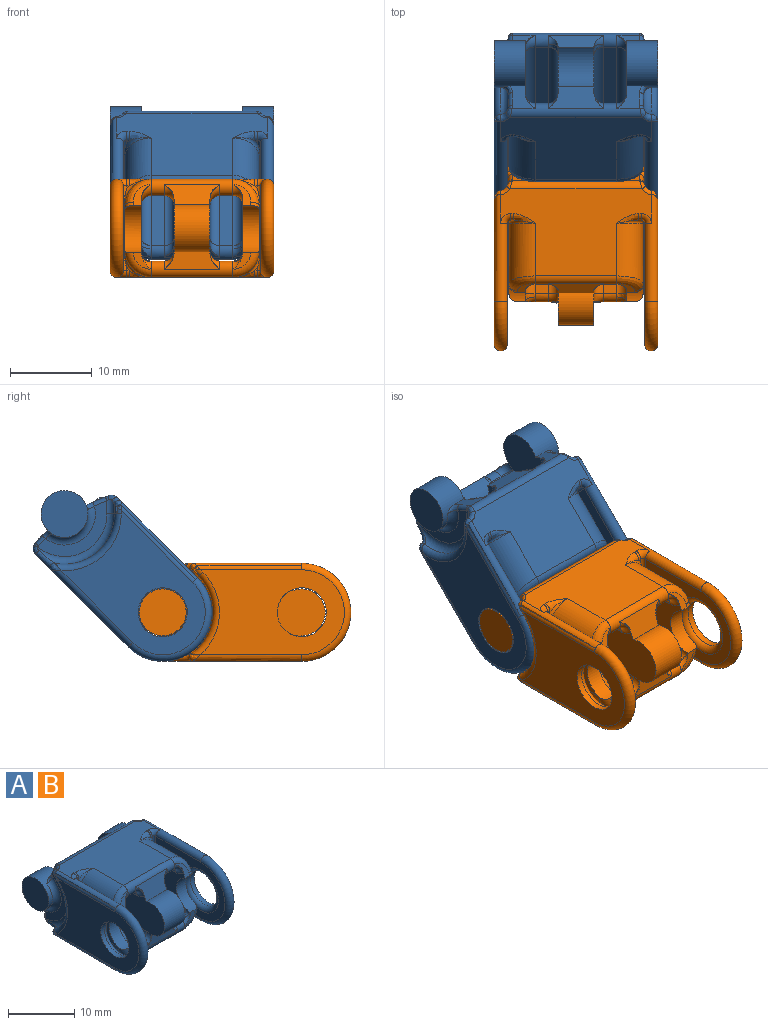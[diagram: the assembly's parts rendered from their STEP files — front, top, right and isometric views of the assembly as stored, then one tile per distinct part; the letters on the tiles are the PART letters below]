
ASSEMBLY  parts=2 mates=1
PART A: 156 faces, bbox 21.1x27x14.7 mm
  f0: plane 0.41x0.32mm, normal (0,-1,0), area 0.1mm2, adj f66,f67,f81
  f1: plane 7.26x3.08mm, normal (0,0.92,0.38), area 14mm2, adj f10,f27,f30,f47,f91,f119
  f2: plane 3.54x2.61mm, normal (0,1,0), area 4.2mm2, adj f12,f21,f29,f41,f56,f57
  f3: plane 2.19x2mm, normal (0,-1,0), area 1.8mm2, adj f5,f23,f37,f52
  f4: plane 3.08x2.66mm, normal (0,-0.92,0.38), area 2.5mm2, adj f12,f23,f42,f50,f51
  f5: plane 0.09x0.04mm, normal (-1,0,0), area 0mm2, adj f3,f23,f37
  f6: plane 0.09x0.04mm, normal (1,0,0), area 0mm2, adj f8,f27,f35
  f7: plane 7.26x2.6mm, normal (0,-1,0), area 11mm2, adj f10,f25,f31,f32,f91,f104
  f8: plane 6.8x2mm, normal (0,1,0), area 10.4mm2, adj f6,f27,f29,f35,f89,f107
  f9: plane 3.54x3.21mm, normal (0,0.92,0.38), area 5.5mm2, adj f12,f21,f30,f44,f61,f62,f63
  f10: plane 18.78x6.61mm, normal (1,0,0), area 95.3mm2, adj f1,f7,f25,f26,f27,f32,f33,f45
  f11: plane 8.52x5.6mm, normal (1,0,0), area 39.6mm2, adj f23,f48,f49,f51,f68
  f12: plane 18.78x6.61mm, normal (-1,0,0), area 95.3mm2, adj f2,f4,f9,f21,f23,f40,f41,f42
  f13: plane 14.8x10.4mm, normal (-1,0,0), area 96.9mm2, adj f67,f75,f77,f79,f83
  f14: plane 19.08x15.68mm, normal (0,0,-1), area 190.7mm2, adj f29,f31,f48,f60,f79,f80,f81,f82
  f15: plane 5.72x5.72mm, normal (1,0,0), area 25.7mm2, adj f21
  f16: plane 19.08x11.37mm, normal (0,0,1), area 134.3mm2, adj f28,f30,f49,f65,f70,f71,f74,f75
  f17: plane 10.69x1.6mm, normal (0,0,-1), area 17.1mm2, adj f28,f30,f43,f46
  f18: plane 17.6x10.4mm, normal (1,0,0), area 126.3mm2, adj f24,f73,f75,f76,f77,f79
  f19: plane 0.41x0.32mm, normal (0,-1,0), area 0.1mm2, adj f67,f69,f71
  f20: plane 15x1.6mm, normal (0,0,1), area 24mm2, adj f29,f31,f33,f34,f39,f40
  f21: cylinder r=2.86mm len=5.72mm, axis (1,0,0), area 45.4mm2, adj f2,f9,f12,f15,f55,f56,f61
  f22: plane 9.99x4.7mm, normal (1,0,0), area 16mm2, adj f53,f54,f55,f57,f58,f62
  f23: cylinder r=3mm len=5.77mm, axis (1,0,0), area 16.1mm2, adj f3,f4,f5,f11,f12,f38,f39,f48
  f24: cylinder r=3mm len=6mm, axis (1,0,0), area 15.1mm2, adj f18,f83
  f25: cylinder r=2.86mm len=5.72mm, axis (-1,0,0), area 44.5mm2, adj f7,f10,f26,f91
  f26: plane 7.26x3.2mm, normal (0,-0.92,0.38), area 14.6mm2, adj f10,f25,f28,f45,f91,f117
  f27: cylinder r=3mm len=5.77mm, axis (-1,0,0), area 36.3mm2, adj f1,f6,f8,f10,f34,f36,f89,f91
  f28: cylinder r=1mm len=10mm, axis (-1,0,0), area 18.1mm2, adj f16,f17,f26,f42,f45,f50,f96,f114
  f29: cylinder r=1mm len=15.63mm, axis (-1,0,0), area 29.5mm2, adj f2,f8,f14,f20,f35,f36,f41,f58
  f30: cylinder r=1mm len=16.18mm, axis (1,0,0), area 25mm2, adj f1,f9,f16,f17,f44,f47,f64,f90
  f31: cylinder r=1mm len=10mm, axis (-1,0,0), area 20.7mm2, adj f7,f14,f20,f32,f37,f38,f52,f99
  f32: torus R=2.2mm, axis (-1,0,0), area 2.5mm2, adj f7,f10,f31,f33
  f33: cylinder r=1.2mm len=14.92mm, axis (0,1,0), area 28.1mm2, adj f10,f20,f32,f34
  f34: bspline ~1.28x1.26mm, area 0.1mm2, adj f20,f27,f33,f36
  f35: torus R=2.2mm, axis (-1,0,0), area 1.1mm2, adj f6,f8,f29,f36
  f36: bspline ~1.41x1.35mm, area 1.1mm2, adj f27,f29,f34,f35
  f37: torus R=2.2mm, axis (-1,0,0), area 1.1mm2, adj f3,f5,f31,f38
  f38: bspline ~1.41x1.35mm, area 1.1mm2, adj f23,f31,f37,f39
  f39: bspline ~1.28x1.26mm, area 0.1mm2, adj f20,f23,f38,f40
  f40: cylinder r=1.2mm len=14.92mm, axis (0,-1,0), area 28.1mm2, adj f12,f20,f39,f41
  f41: torus R=2.2mm, axis (-1,0,0), area 2.5mm2, adj f2,f12,f29,f40
  f42: torus R=2.2mm, axis (-1,0,0), area 3.6mm2, adj f4,f12,f28,f43
  f43: cylinder r=1.2mm len=10.69mm, axis (0,1,0), area 20.2mm2, adj f12,f17,f42,f44
  f44: torus R=2.2mm, axis (-1,0,0), area 3.6mm2, adj f9,f12,f30,f43
  f45: torus R=2.2mm, axis (-1,0,0), area 3.6mm2, adj f10,f26,f28,f46
  f46: cylinder r=1.2mm len=10.69mm, axis (0,-1,0), area 20.2mm2, adj f10,f17,f45,f47
  f47: torus R=2.2mm, axis (-1,0,0), area 3.6mm2, adj f1,f10,f30,f46
  f48: cylinder r=3.2mm len=8.6mm, axis (0,1,0), area 43.2mm2, adj f11,f14,f23,f52,f66
  f49: cylinder r=3.2mm len=7.36mm, axis (0,-1,0), area 34.7mm2, adj f11,f16,f50,f69
  f50: bspline ~3.78x3.76mm, area 6mm2, adj f4,f28,f49,f51
  f51: cylinder r=1mm len=1.16mm, axis (0,0.38,0.92), area 0.8mm2, adj f4,f11,f23,f50
  f52: torus R=2.2mm, axis (0,-1,0), area 6.8mm2, adj f3,f23,f31,f48
  f53: torus R=5.2mm, axis (1,0,0), area 16.5mm2, adj f22,f54,f59,f60,f76
  f54: cylinder r=0.94mm len=1.91mm, axis (0,-0.71,-0.71), area 2.3mm2, adj f22,f53,f63,f64,f65,f73
  f55: torus R=3.8mm, axis (1,0,0), area 11.4mm2, adj f21,f22,f56,f61
  f56: bspline ~1.79x1.7mm, area 1mm2, adj f2,f21,f55,f57
  f57: cylinder r=0.5mm len=1.23mm, axis (0,0,1), area 1mm2, adj f2,f22,f56,f58
  f58: torus R=0.5mm, axis (1,0,0), area 0.2mm2, adj f22,f29,f57,f59
  f59: bspline ~1.21x0.9mm, area 0.8mm2, adj f29,f53,f58,f60
  f60: bspline ~3.69x1.74mm, area 3mm2, adj f14,f53,f59,f78
  f61: bspline ~1.7x1.65mm, area 1mm2, adj f9,f21,f55,f62
  f62: cylinder r=0.5mm len=1.72mm, axis (0,-0.38,0.92), area 1.3mm2, adj f9,f22,f61,f63
  f63: bspline ~0.57x0.53mm, area 0.3mm2, adj f9,f54,f62,f64
  f64: bspline ~1.18x1.16mm, area 0.7mm2, adj f30,f54,f63,f65
  f65: bspline ~1.11x0.99mm, area 1.1mm2, adj f16,f54,f64,f72
  f66: torus R=3.6mm, axis (0,-1,0), area 1.9mm2, adj f0,f48,f67,f68,f82
  f67: cylinder r=0.4mm len=10.4mm, axis (0,0,1), area 4mm2, adj f0,f13,f19,f66,f68,f69,f74,f80
  f68: cylinder r=0.4mm len=5.6mm, axis (0,0,1), area 1.6mm2, adj f11,f66,f67,f69
  f69: torus R=3.6mm, axis (0,-1,0), area 1.9mm2, adj f19,f49,f67,f68,f70
  f70: bspline ~3.09x1.2mm, area 1.2mm2, adj f16,f69,f71
  f71: cylinder r=0.8mm len=0.8mm, axis (-1,0,0), area 0.4mm2, adj f16,f19,f70,f74
  f72: bspline ~1.93x0.98mm, area 0.8mm2, adj f65,f73,f75
  f73: cylinder r=0.8mm len=1.37mm, axis (0,-0.71,-0.71), area 1mm2, adj f18,f54,f72,f76
  f74: torus R=1.2mm, axis (0,0,1), area 1.4mm2, adj f16,f67,f71,f75
  f75: cylinder r=0.8mm len=13.11mm, axis (0,-1,0), area 28.1mm2, adj f13,f16,f18,f72,f74,f77
  f76: torus R=6.94mm, axis (-1,0,0), area 13.7mm2, adj f18,f53,f73,f78
  f77: torus R=5.2mm, axis (-1,0,0), area 45.1mm2, adj f13,f18,f75,f79
  f78: bspline ~2.51x1.15mm, area 1mm2, adj f60,f76,f79
  f79: cylinder r=0.8mm len=13.28mm, axis (0,1,0), area 28.2mm2, adj f13,f14,f18,f77,f78,f80
  f80: torus R=1.2mm, axis (0,0,1), area 1.4mm2, adj f14,f67,f79,f81
  f81: cylinder r=0.8mm len=0.8mm, axis (1,0,0), area 0.4mm2, adj f0,f14,f80,f82
  f82: bspline ~3.09x1.2mm, area 1.1mm2, adj f14,f66,f81
  f83: torus R=3.8mm, axis (-1,0,0), area 26mm2, adj f13,f24
  f84: plane 0.41x0.32mm, normal (0,-1,0), area 0.1mm2, adj f138,f139,f153
  f85: plane 3.54x2.61mm, normal (0,1,0), area 4.2mm2, adj f29,f93,f100,f113,f128,f129
  f86: plane 2.19x2mm, normal (0,-1,0), area 1.8mm2, adj f88,f102,f109,f124
  f87: plane 3.08x2.66mm, normal (0,-0.92,0.38), area 2.5mm2, adj f93,f102,f114,f122,f123
  f88: plane 0.09x0.04mm, normal (1,0,0), area 0mm2, adj f86,f102,f109
  f89: plane 0.09x0.04mm, normal (-1,0,0), area 0mm2, adj f8,f27,f107
  f90: plane 3.54x3.21mm, normal (0,0.92,0.38), area 5.5mm2, adj f30,f93,f100,f116,f133,f134,f135
  f91: plane 18.78x6.61mm, normal (-1,0,0), area 95.3mm2, adj f1,f7,f25,f26,f27,f104,f105,f117
  f92: plane 8.52x5.6mm, normal (-1,0,0), area 39.6mm2, adj f102,f120,f121,f123,f140
  f93: plane 18.78x6.61mm, normal (1,0,0), area 95.3mm2, adj f85,f87,f90,f100,f102,f112,f113,f114
  f94: plane 14.8x10.4mm, normal (1,0,0), area 96.9mm2, adj f139,f147,f149,f151,f155
  f95: plane 5.72x5.72mm, normal (-1,0,0), area 25.7mm2, adj f100
  f96: plane 10.69x1.6mm, normal (0,0,-1), area 17.1mm2, adj f28,f30,f115,f118
  f97: plane 17.6x10.4mm, normal (-1,0,0), area 126.3mm2, adj f103,f145,f147,f148,f149,f151
  f98: plane 0.41x0.32mm, normal (0,-1,0), area 0.1mm2, adj f139,f141,f143
  f99: plane 15x1.6mm, normal (0,0,1), area 24mm2, adj f29,f31,f105,f106,f111,f112
  f100: cylinder r=2.86mm len=5.72mm, axis (-1,0,0), area 45.4mm2, adj f85,f90,f93,f95,f127,f128,f133
  f101: plane 9.99x4.7mm, normal (-1,0,0), area 16mm2, adj f125,f126,f127,f129,f130,f134
  f102: cylinder r=3mm len=5.77mm, axis (-1,0,0), area 16.1mm2, adj f86,f87,f88,f92,f93,f110,f111,f120
  f103: cylinder r=3mm len=6mm, axis (-1,0,0), area 15.1mm2, adj f97,f155
  f104: torus R=2.2mm, axis (1,0,0), area 2.5mm2, adj f7,f31,f91,f105
  f105: cylinder r=1.2mm len=14.92mm, axis (0,1,0), area 28.1mm2, adj f91,f99,f104,f106
  f106: bspline ~1.28x1.26mm, area 0.1mm2, adj f27,f99,f105,f108
  f107: torus R=2.2mm, axis (1,0,0), area 1.1mm2, adj f8,f29,f89,f108
  f108: bspline ~1.41x1.35mm, area 1.1mm2, adj f27,f29,f106,f107
  f109: torus R=2.2mm, axis (1,0,0), area 1.1mm2, adj f31,f86,f88,f110
  f110: bspline ~1.41x1.35mm, area 1.1mm2, adj f31,f102,f109,f111
  f111: bspline ~1.28x1.26mm, area 0.1mm2, adj f99,f102,f110,f112
  f112: cylinder r=1.2mm len=14.92mm, axis (0,-1,0), area 28.1mm2, adj f93,f99,f111,f113
  f113: torus R=2.2mm, axis (1,0,0), area 2.5mm2, adj f29,f85,f93,f112
  f114: torus R=2.2mm, axis (1,0,0), area 3.6mm2, adj f28,f87,f93,f115
  f115: cylinder r=1.2mm len=10.69mm, axis (0,1,0), area 20.2mm2, adj f93,f96,f114,f116
  f116: torus R=2.2mm, axis (1,0,0), area 3.6mm2, adj f30,f90,f93,f115
  f117: torus R=2.2mm, axis (1,0,0), area 3.6mm2, adj f26,f28,f91,f118
  f118: cylinder r=1.2mm len=10.69mm, axis (0,-1,0), area 20.2mm2, adj f91,f96,f117,f119
  f119: torus R=2.2mm, axis (1,0,0), area 3.6mm2, adj f1,f30,f91,f118
  f120: cylinder r=3.2mm len=8.6mm, axis (0,1,0), area 43.2mm2, adj f14,f92,f102,f124,f138
  f121: cylinder r=3.2mm len=7.36mm, axis (0,-1,0), area 34.7mm2, adj f16,f92,f122,f141
  f122: bspline ~3.78x3.76mm, area 6mm2, adj f28,f87,f121,f123
  f123: cylinder r=1mm len=1.16mm, axis (0,0.38,0.92), area 0.8mm2, adj f87,f92,f102,f122
  f124: torus R=2.2mm, axis (0,-1,0), area 6.8mm2, adj f31,f86,f102,f120
  f125: torus R=5.2mm, axis (-1,0,0), area 16.5mm2, adj f101,f126,f131,f132,f148
  f126: cylinder r=0.94mm len=1.91mm, axis (0,-0.71,-0.71), area 2.3mm2, adj f101,f125,f135,f136,f137,f145
  f127: torus R=3.8mm, axis (-1,0,0), area 11.4mm2, adj f100,f101,f128,f133
  f128: bspline ~1.79x1.7mm, area 1mm2, adj f85,f100,f127,f129
  f129: cylinder r=0.5mm len=1.23mm, axis (0,0,1), area 1mm2, adj f85,f101,f128,f130
  f130: torus R=0.5mm, axis (-1,0,0), area 0.2mm2, adj f29,f101,f129,f131
  f131: bspline ~1.21x0.9mm, area 0.8mm2, adj f29,f125,f130,f132
  f132: bspline ~3.69x1.74mm, area 3mm2, adj f14,f125,f131,f150
  f133: bspline ~1.7x1.65mm, area 1mm2, adj f90,f100,f127,f134
  f134: cylinder r=0.5mm len=1.72mm, axis (0,-0.38,0.92), area 1.3mm2, adj f90,f101,f133,f135
  f135: bspline ~0.85x0.59mm, area 0.3mm2, adj f90,f126,f134,f136
  f136: bspline ~1.18x1.16mm, area 0.7mm2, adj f30,f126,f135,f137
  f137: bspline ~1.11x0.99mm, area 1.1mm2, adj f16,f126,f136,f144
  f138: torus R=3.6mm, axis (0,-1,0), area 1.9mm2, adj f84,f120,f139,f140,f154
  f139: cylinder r=0.4mm len=10.4mm, axis (0,0,1), area 4mm2, adj f84,f94,f98,f138,f140,f141,f146,f152
  f140: cylinder r=0.4mm len=5.6mm, axis (0,0,1), area 1.6mm2, adj f92,f138,f139,f141
  f141: torus R=3.6mm, axis (0,-1,0), area 1.9mm2, adj f98,f121,f139,f140,f142
  f142: bspline ~3.09x1.2mm, area 1.1mm2, adj f16,f141,f143
  f143: cylinder r=0.8mm len=0.8mm, axis (1,0,0), area 0.4mm2, adj f16,f98,f142,f146
  f144: bspline ~1.93x0.98mm, area 0.8mm2, adj f137,f145,f147
  f145: cylinder r=0.8mm len=1.37mm, axis (0,-0.71,-0.71), area 1mm2, adj f97,f126,f144,f148
  f146: torus R=1.2mm, axis (0,0,1), area 1.4mm2, adj f16,f139,f143,f147
  f147: cylinder r=0.8mm len=13.11mm, axis (0,-1,0), area 28.1mm2, adj f16,f94,f97,f144,f146,f149
  f148: torus R=6.94mm, axis (1,0,0), area 13.7mm2, adj f97,f125,f145,f150
  f149: torus R=5.2mm, axis (1,0,0), area 45.1mm2, adj f94,f97,f147,f151
  f150: bspline ~2.51x1.15mm, area 1mm2, adj f132,f148,f151
  f151: cylinder r=0.8mm len=13.28mm, axis (0,1,0), area 28.2mm2, adj f14,f94,f97,f149,f150,f152
  f152: torus R=1.2mm, axis (0,0,1), area 1.4mm2, adj f14,f139,f151,f153
  f153: cylinder r=0.8mm len=0.8mm, axis (-1,0,0), area 0.4mm2, adj f14,f84,f152,f154
  f154: bspline ~3.09x1.2mm, area 1.1mm2, adj f14,f138,f153
  f155: torus R=3.8mm, axis (1,0,0), area 26mm2, adj f94,f103
PART B: same geometry as A
PLACE A rot(axis=(1,0,0),45deg) t=(0,18.31,8.83)mm
PLACE B at identity fixed
MATE revolute B.f125 <-> A.f149  axis (1,0,0) through (10,7,6)mm
